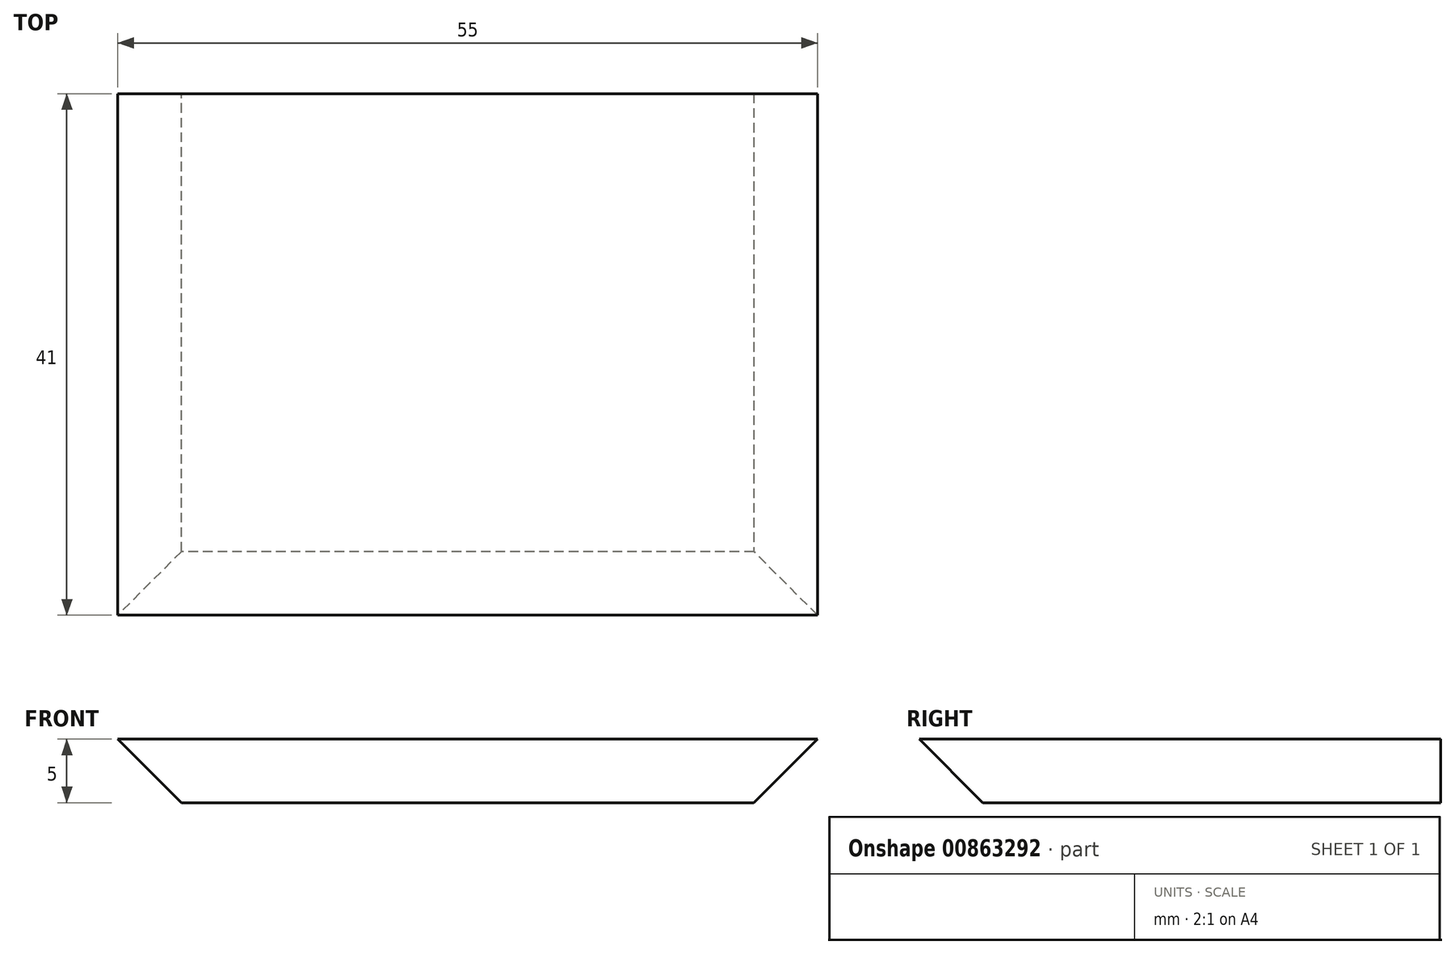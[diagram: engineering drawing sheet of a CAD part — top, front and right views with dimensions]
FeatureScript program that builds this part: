
annotation { "Feature Type Name" : "Feature", "Feature Type Description" : "" }
export const myFeature = defineFeature(function(context is Context, id is Id, definition is map)
    precondition{}
    {
        {
            var Q0;
            Q0=qCreatedBy(makeId("Top.planeOp"),FACE);
            var sketch = newSketch(context, id + "F0", { "sketchPlane" : qUnion([Q0])});
            skLineSegment(sketch, "E0.bottom", {"start": v(27.5, -52.5) * mm, "end": v(-27.5, -52.5) * mm});
            skLineSegment(sketch, "E0.top", {"start": v(27.5, 52.5) * mm, "end": v(-27.5, 52.5) * mm});
            skLineSegment(sketch, "E0.left", {"start": v(27.5, -52.5) * mm, "end": v(27.5, 52.5) * mm});
            skLineSegment(sketch, "E0.right", {"start": v(-27.5, -52.5) * mm, "end": v(-27.5, 52.5) * mm});
            skPoint(sketch, "E0.middle", {"position": v(0, 0) * mm});
            skLineSegment(sketch, "E1", {"start": v(27.5, -14.74) * mm, "end": v(-27.5, -11.5) * mm});
            skLineSegment(sketch, "E2", {"start": v(-27.5, -11.5) * mm, "end": v(27.5, -11.5) * mm});
            skSolve(sketch);
        }
        {
            var Q0;
            {var subQ0=sQuery(id+"F0.wireOp",EDGE,"E0.bottom");Q0=makeQuery(id+"F0.imprint","IMPRINT",FACE,{"disambiguationData":[TD([[makeQuery(id+"F0.imprint","IMPRINT",EDGE,{"derivedFrom":subQ0}),-1.0]])]});}
            var Q1;
            {var subQ0=sQuery(id+"F0.wireOp",EDGE,"E1");Q1=makeQuery(id+"F0.imprint","IMPRINT",FACE,{"disambiguationData":[TD([[makeQuery(id+"F0.imprint","IMPRINT",EDGE,{"derivedFrom":subQ0}),-1.0]])]});}
            extrude(context, id + "F1", {"entities" : qUnion([Q0, Q1]), "depth" : 5 * mm, "offsetDistance" : 25 * mm});
        }
        {
            var Q0;
            Q0=makeQuery(id+"F1.opExtrude","CAP_EDGE",EDGE,{"disambiguationData":[OSD([sQuery(id+"F0.wireOp",EDGE,"E0.right")])],"isStart":true});
            var Q1;
            Q1=makeQuery(id+"F1.opExtrude","CAP_EDGE",EDGE,{"disambiguationData":[OSD([sQuery(id+"F0.wireOp",EDGE,"E0.bottom")])],"isStart":true});
            var Q2;
            Q2=makeQuery(id+"F1.opExtrude","CAP_EDGE",EDGE,{"disambiguationData":[OSD([sQuery(id+"F0.wireOp",EDGE,"E0.left")])],"isStart":true});
            chamfer(context, id + "F2", {"entities" : qUnion([Q0, Q1, Q2]), "width" : 5 * mm, "tangentPropagation" : true});
        }
    });
